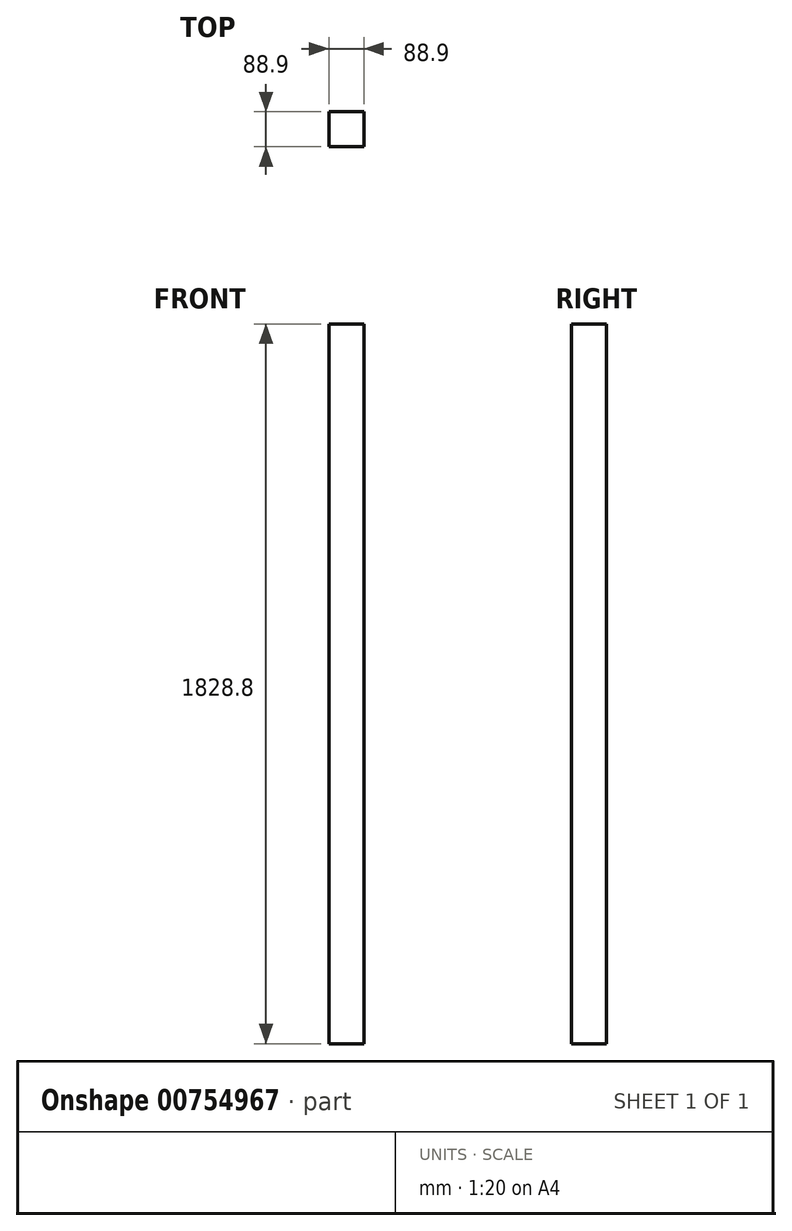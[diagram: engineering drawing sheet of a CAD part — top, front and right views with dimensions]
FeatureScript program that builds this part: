
annotation { "Feature Type Name" : "Feature", "Feature Type Description" : "" }
export const myFeature = defineFeature(function(context is Context, id is Id, definition is map)
    precondition{}
    {
        {
            var Q0;
            Q0=qCreatedBy(makeId("Top.planeOp"),FACE);
            var sketch = newSketch(context, id + "F0", { "sketchPlane" : qUnion([Q0])});
            skLineSegment(sketch, "E0.bottom", {"start": v(0, 88.66) * mm, "end": v(88.9, 88.66) * mm});
            skLineSegment(sketch, "E0.top", {"start": v(0, -0.24) * mm, "end": v(88.9, -0.24) * mm});
            skLineSegment(sketch, "E0.left", {"start": v(0, 88.66) * mm, "end": v(0, -0.24) * mm});
            skLineSegment(sketch, "E0.right", {"start": v(88.9, 88.66) * mm, "end": v(88.9, -0.24) * mm});
            skLineSegment(sketch, "E1.bottom", {"start": v(0, 162.85) * mm, "end": v(0, 162.85) * mm});
            skLineSegment(sketch, "E1.top", {"start": v(0, 88.66) * mm, "end": v(0, 88.66) * mm});
            skLineSegment(sketch, "E1.left", {"start": v(0, 162.85) * mm, "end": v(0, 88.66) * mm, "construction": true});
            skLineSegment(sketch, "E1.right", {"start": v(0, 162.85) * mm, "end": v(0, 88.66) * mm, "construction": true});
            skLineSegment(sketch, "E2.bottom", {"start": v(88.9, 88.66) * mm, "end": v(88.9, 88.66) * mm});
            skLineSegment(sketch, "E2.top", {"start": v(88.9, -0.24) * mm, "end": v(88.9, -0.24) * mm});
            skLineSegment(sketch, "E2.left", {"start": v(88.9, 88.66) * mm, "end": v(88.9, -0.24) * mm, "construction": true});
            skLineSegment(sketch, "E2.right", {"start": v(88.9, 88.66) * mm, "end": v(88.9, -0.24) * mm, "construction": true});
            skSolve(sketch);
        }
        {
            var Q0;
            Q0=makeQuery(id+"F0.imprint","IMPRINT",FACE,{"disambiguationData":[TD([[makeQuery(id+"F0.imprint","IMPRINT",EDGE,{"derivedFrom":sQuery(id+"F0.wireOp",EDGE,"E0.bottom")}),-1.0]])]});
            extrude(context, id + "F1", {"entities" : qUnion([Q0]), "depth" : 1828.8 * mm, "offsetDistance" : 25.4 * mm});
        }
    });
